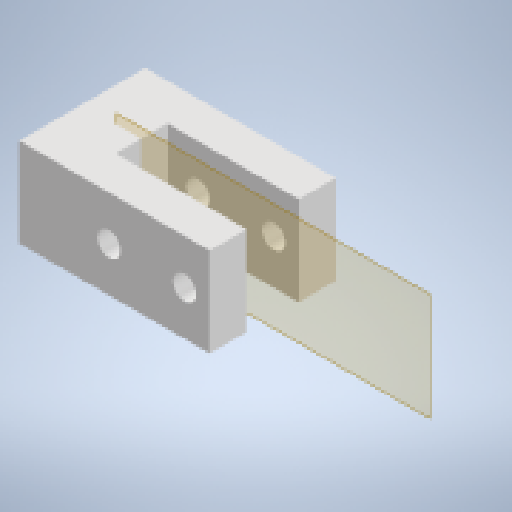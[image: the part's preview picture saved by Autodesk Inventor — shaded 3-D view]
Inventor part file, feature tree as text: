
AUTODESK INVENTOR PART (.ipt)
format: ipt  version: 2024.3 (Build 283343000, 343)  size: 267,264 bytes
history: native  units: mm
features: sketch x11, projected_geometry x8, extrude x6, other x4, plane x3, reference x3, mirror x1, loft x1, sweep x1, chamfer x1
ambient origin geometry x8: Origin, YZ Plane, XZ Plane, XY Plane, X Axis, Y Axis, Z Axis, Center Point
bodies: Solid1 (feature_tree)
feature tree (39):
  sketch  "Sketch1"  dims[d0=5.0mm d1=0.0mm d2=0.2mm d3=0.0mm]
  plane  "Work Plane1"
  extrude  "Extrusion1"  Depth=5.0mm TaperAngle=0.0deg
  mirror  "Mirror1"
  extrude  "Extrusion2"  Depth=8.0mm
  extrude  "Extrusion3"  Depth=12.0mm
  plane  "Work Plane2"
  sketch  "Sketch4"  dims[d11=0.0mm d12=90.0deg d13=0.0mm d14=90.0deg]
  sketch  "Sketch5"  dims[d16=45.748737mm d17=16.248737mm]
  loft  "Loft1"
  sketch  "Sketch6"  dims[d18=0.0mm d19=0.0mm d20=8.0mm d21=0.0mm d22=22.0mm d23=8.0mm d24=45.0deg]
  plane  "Work Plane3"
  sweep  "Sweep1"
  sketch  "Sketch8"  dims[d28=3.0mm d29=0.0mm]
  extrude  "Extrusion4"  Depth=8.0mm TaperAngle=0.0deg
  chamfer  "Chamfer1"  Distance=8.0mm Angle=45.0deg
  extrude  "Extrusion5"  Depth=20.0mm TaperAngle=0.0deg
  extrude  "Extrusion6"  [1 undecoded]
  reference  "Reference1"
  sketch  "Sketch2"  dims[d4=8.0mm d5=0.0mm d6=50.0mm]
  projected_geometry  "Projected Loop1"
  reference  "Reference2"
  projected_geometry  "Projected Loop2"
  sketch  "Sketch3"  dims[d9=17.0mm d10=12.0mm]
  projected_geometry  "Projected Loop3"
  reference  "Reference3"
  projected_geometry  "Projected Loop4"
  projected_geometry  "Projected Loop5"
  projected_geometry  "Projected Loop6"
  other  "Edges1"
  projected_geometry  "Projected Loop7"
  sketch  "Sketch7"  dims[d25=4.0mm d26=20.0mm d27=0.0mm]
  sketch  "Sketch9"
  sketch  "Sketch10"
  sketch  "Sketch11"
  projected_geometry  "Projected Loop8"
  other  "Assembly1"
  other  "dedos:1"
  other  "housing:1"
note: 1 required parameter value undecoded (feature->parameter linkage not recoverable at this tier; creation-order binding heuristic only, values carry confidence <= 0.55)
